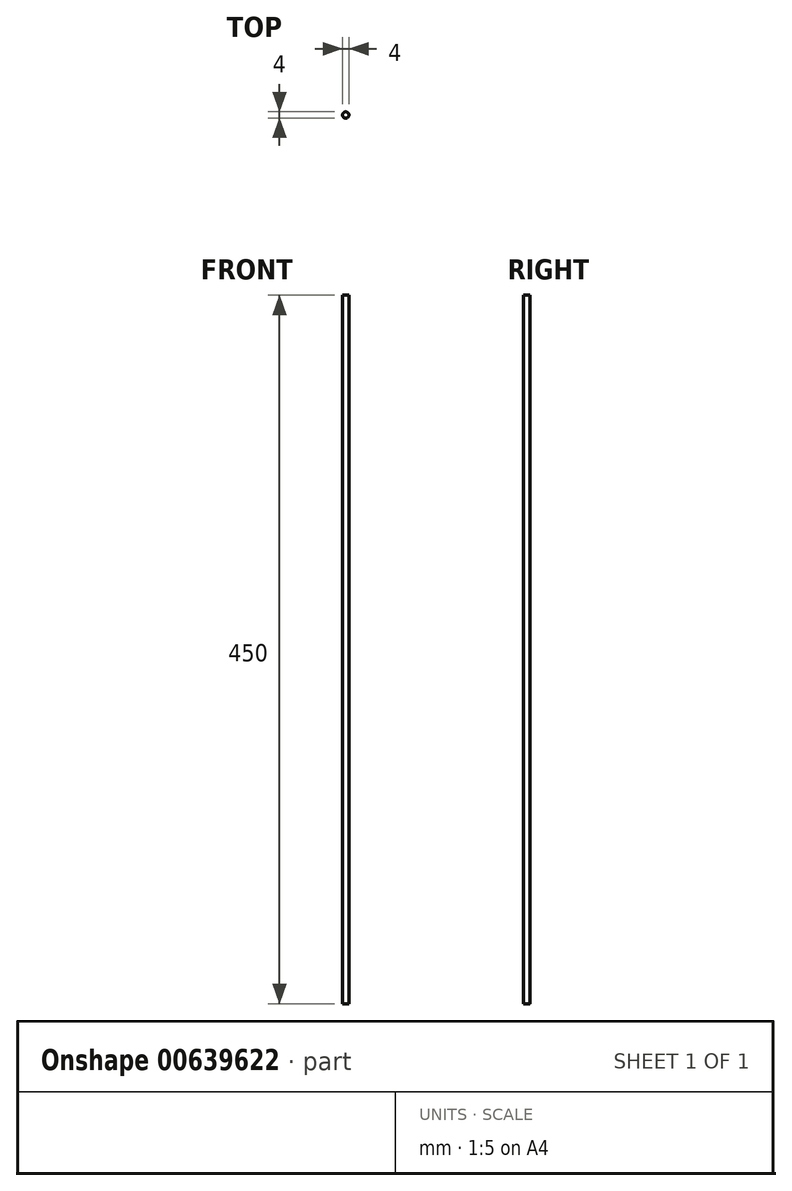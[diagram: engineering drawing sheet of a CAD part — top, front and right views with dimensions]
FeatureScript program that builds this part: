
annotation { "Feature Type Name" : "Feature", "Feature Type Description" : "" }
export const myFeature = defineFeature(function(context is Context, id is Id, definition is map)
    precondition{}
    {
        {
            var Q0;
            Q0=qCreatedBy(makeId("Top.planeOp"),FACE);
            var sketch = newSketch(context, id + "F0", { "sketchPlane" : qUnion([Q0])});
            skCircle(sketch, "E0", {"center": v(0, 0) * mm, "radius": 2 * mm});
            skSolve(sketch);
        }
        {
            var Q0;
            Q0=makeQuery(id+"F0.imprint","IMPRINT",FACE,{"disambiguationData":[TD([[makeQuery(id+"F0.imprint","IMPRINT",EDGE,{"derivedFrom":sQuery(id+"F0.wireOp",EDGE,"E0")}),1.0]])]});
            extrude(context, id + "F1", {"entities" : qUnion([Q0]), "endBound" : BoundingType.SYMMETRIC, "depth" : 450 * mm, "offsetDistance" : 25 * mm});
        }
    });
